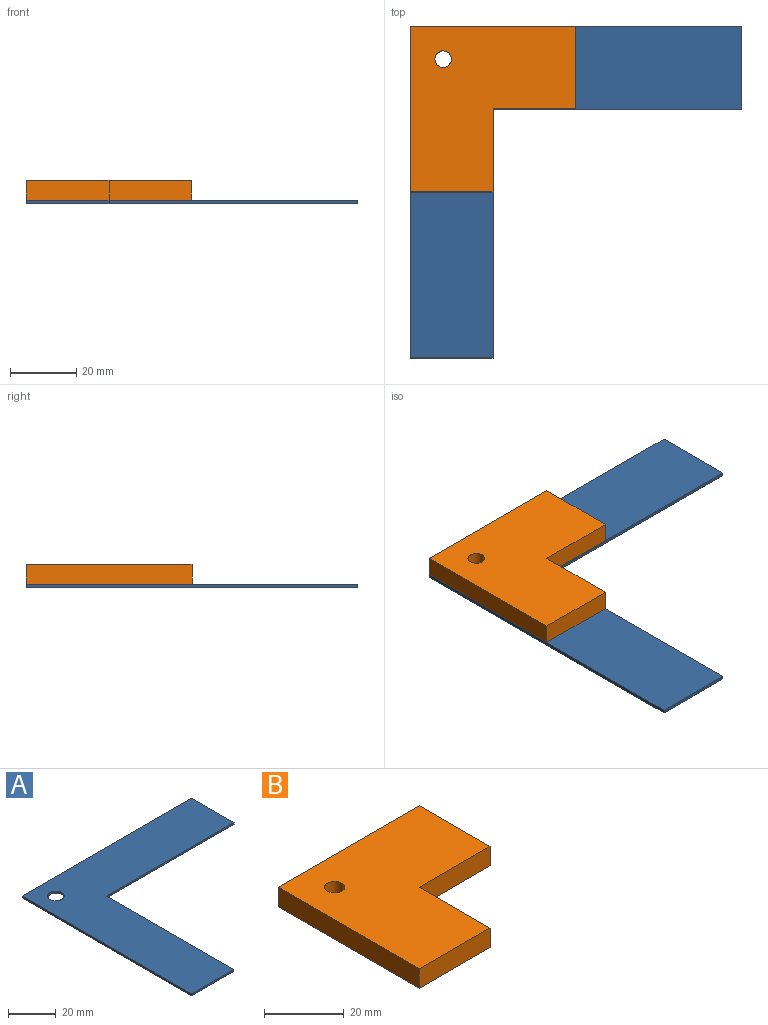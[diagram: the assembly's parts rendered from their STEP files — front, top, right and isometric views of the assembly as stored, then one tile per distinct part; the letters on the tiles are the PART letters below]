
ASSEMBLY  parts=2 mates=1
PART A: 9 faces, bbox 100x100x1 mm
  f0: plane 100x1mm, normal (0,1,0), area 100mm2, adj f1,f5,f6,f7
  f1: plane 100x1mm, normal (-1,0,0), area 100mm2, adj f0,f2,f6,f7
  f2: plane 25x1mm, normal (0,-1,0), area 25mm2, adj f1,f3,f6,f7
  f3: plane 75x1mm, normal (1,0,0), area 75mm2, adj f2,f4,f6,f7
  f4: plane 75x1mm, normal (0,-1,0), area 75mm2, adj f3,f5,f6,f7
  f5: plane 25x1mm, normal (1,0,0), area 25mm2, adj f0,f4,f6,f7
  f6: plane 100x100mm, normal (0,0,1), area 4336.5mm2, adj f0,f1,f2,f3,f4,f5,f8
  f7: plane 100x100mm, normal (0,0,-1), area 4336.5mm2, adj f0,f1,f2,f3,f4,f5,f8
  f8: cylinder r=3.5mm len=7mm, axis (0,0,1), area 22mm2, adj f6,f7
PART B: 9 faces, bbox 50x50x6 mm
  f0: plane 50x6mm, normal (0,1,0), area 300mm2, adj f1,f5,f6,f7
  f1: plane 50x6mm, normal (-1,0,0), area 300mm2, adj f0,f2,f6,f7
  f2: plane 25x6mm, normal (0,-1,0), area 150mm2, adj f1,f3,f6,f7
  f3: plane 25x6mm, normal (1,0,0), area 150mm2, adj f2,f4,f6,f7
  f4: plane 25x6mm, normal (0,-1,0), area 150mm2, adj f3,f5,f6,f7
  f5: plane 25x6mm, normal (1,0,0), area 150mm2, adj f0,f4,f6,f7
  f6: plane 50x50mm, normal (0,0,1), area 1855.4mm2, adj f0,f1,f2,f3,f4,f5,f8
  f7: plane 50x50mm, normal (0,0,-1), area 1855.4mm2, adj f0,f1,f2,f3,f4,f5,f8
  f8: cylinder r=2.5mm len=6mm, axis (0,0,1), area 94.2mm2, adj f6,f7
PLACE A at identity
PLACE B t=(0,0,1)mm
MATE fastened B.f7 <-> A.f6  axis (0,0,1) through (25,-25,1)mm
